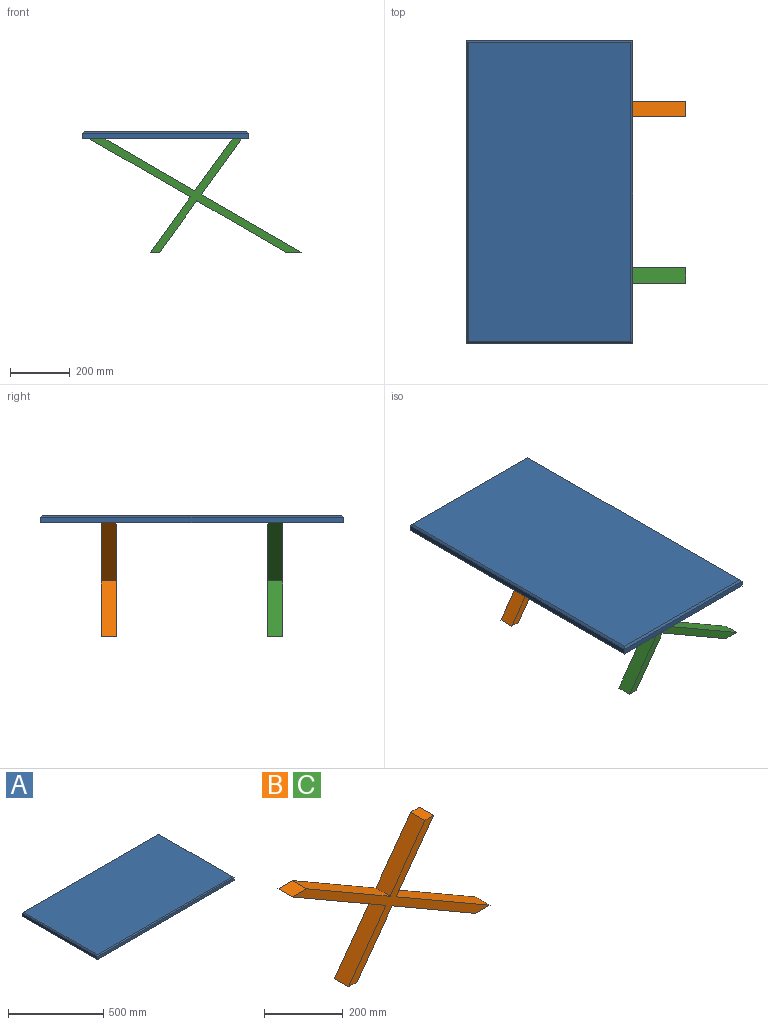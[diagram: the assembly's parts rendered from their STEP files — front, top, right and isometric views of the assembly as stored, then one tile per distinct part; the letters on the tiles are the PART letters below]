
ASSEMBLY  parts=3 mates=1
PART A: 10 faces, bbox 1016x558.8x25.4 mm
  f0: plane 1016x19.05mm, normal (0,1,0), area 19354.8mm2, adj f1,f3,f5,f9
  f1: plane 558.8x19.05mm, normal (-1,0,0), area 10645.1mm2, adj f0,f2,f5,f7
  f2: plane 1016x19.05mm, normal (0,-1,0), area 19354.8mm2, adj f1,f3,f5,f6
  f3: plane 558.8x19.05mm, normal (1,0,0), area 10645.1mm2, adj f0,f2,f5,f8
  f4: plane 1003.3x546.1mm, normal (0,0,1), area 547902.1mm2, adj f6,f7,f8,f9
  f5: plane 1016x558.8mm, normal (0,0,-1), area 567740.8mm2, adj f0,f1,f2,f3
  f6: plane 1016x6.35mm, normal (0,-0.71,0.71), area 9066.9mm2, adj f2,f4,f7,f8
  f7: plane 558.8x6.35mm, normal (-0.71,0,0.71), area 4961.1mm2, adj f1,f4,f6,f9
  f8: plane 558.8x6.35mm, normal (0.71,0,0.71), area 4961.1mm2, adj f3,f4,f6,f9
  f9: plane 1016x6.35mm, normal (0,0.71,0.71), area 9066.9mm2, adj f0,f4,f7,f8
PART B: 14 faces, bbox 710.7x50.8x381 mm
  f0: plane 336.85x194.48mm, normal (-0.5,0,-0.87), area 19759.2mm2, adj f1,f11,f12,f13
  f1: plane 186.52x134.14mm, normal (-0.81,0,0.58), area 11671mm2, adj f0,f2,f12,f13
  f2: plane 50.8x31.29mm, normal (0,0,-1), area 1589.3mm2, adj f1,f3,f12,f13
  f3: plane 173.76x124.96mm, normal (0.81,0,-0.58), area 10872.4mm2, adj f2,f4,f12,f13
  f4: plane 300.95x173.76mm, normal (-0.5,0,-0.87), area 17653.6mm2, adj f3,f5,f12,f13
  f5: plane 50.8x50.8mm, normal (0,0,-1), area 2580.6mm2, adj f4,f6,f12,f13
  f6: plane 336.85x194.48mm, normal (0.5,0,0.87), area 19759.2mm2, adj f5,f7,f12,f13
  f7: plane 186.52x134.14mm, normal (0.81,0,-0.58), area 11671mm2, adj f6,f8,f12,f13
  f8: plane 50.8x31.29mm, normal (0,0,1), area 1589.3mm2, adj f7,f9,f12,f13
  f9: plane 173.76x124.96mm, normal (-0.81,0,0.58), area 10872.4mm2, adj f8,f10,f12,f13
  f10: plane 300.95x173.76mm, normal (0.5,0,0.87), area 17653.6mm2, adj f9,f11,f12,f13
  f11: plane 50.8x50.8mm, normal (0,0,1), area 2580.6mm2, adj f0,f10,f12,f13
  f12: plane 710.71x381mm, normal (0,-1,0), area 30626.5mm2, adj f0,f1,f2,f3,f4,f5,f6,f7
  f13: plane 710.71x381mm, normal (0,1,0), area 30626.5mm2, adj f0,f1,f2,f3,f4,f5,f6,f7
PART C: same geometry as B
PLACE A rot(axis=(0,0,1),90deg) t=(204.56,-38.78,317.1)mm
PLACE B t=(-126.13,774.02,-63.9)mm
PLACE C t=(-126.13,215.22,-63.9)mm
MATE fastened B.f8 <-> A.f5  axis (0,0,1) through (179.16,774.02,317.1)mm
